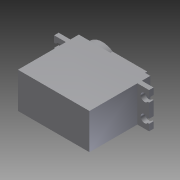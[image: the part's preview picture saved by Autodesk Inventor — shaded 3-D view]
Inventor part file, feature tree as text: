
AUTODESK INVENTOR PART (.ipt)
format: ipt  version: 2012 (Build 160160000, 160)  size: 168,448 bytes
history: native  units: mm
features: extrude x7, sketch x7
ambient origin geometry x8: Origin, YZ Plane, XZ Plane, XY Plane, X Axis, Y Axis, Z Axis, Center Point
bodies: Solid1 (feature_tree)
feature tree (14):
  extrude  "Extrusion1"  Depth=37.0mm
  extrude  "Extrusion2"  Depth=2.5mm
  extrude  "Extrusion3"  Depth=6.5mm TaperAngle=0.0deg
  extrude  "Extrusion4"  Depth=2.5mm
  extrude  "Extrusion5"  Depth=6.5mm TaperAngle=0.0deg
  extrude  "Extrusion6"  Depth=1.2mm
  extrude  "Extrusion7"  Depth=6.5mm TaperAngle=0.0deg
  sketch  "Sketch1"  dims[d0=39.7mm d1=37.0mm]
  sketch  "Sketch2"  dims[d2=19.8mm d3=0.0mm d4=2.5mm]
  sketch  "Sketch3"  dims[d5=10.4mm d6=6.5mm d7=0.0mm]
  sketch  "Sketch4"  dims[d16=6.5mm d17=0.0mm d18=2.5mm]
  sketch  "Sketch5"  dims[d19=10.4mm d20=6.5mm d21=0.0mm]
  sketch  "Sketch6"  dims[d25=4.3mm d26=1.2mm]
  sketch  "Sketch7"  dims[d27=2.4mm d28=6.5mm d29=0.0mm d30=5.0mm d31=19.8mm d32=9.9mm d33=9.9mm d34=3.3mm d35=0.0mm d36=2.0mm d37=2.0mm d38=4.9mm d39=5.0mm d40=3.2mm d41=0.0mm]
